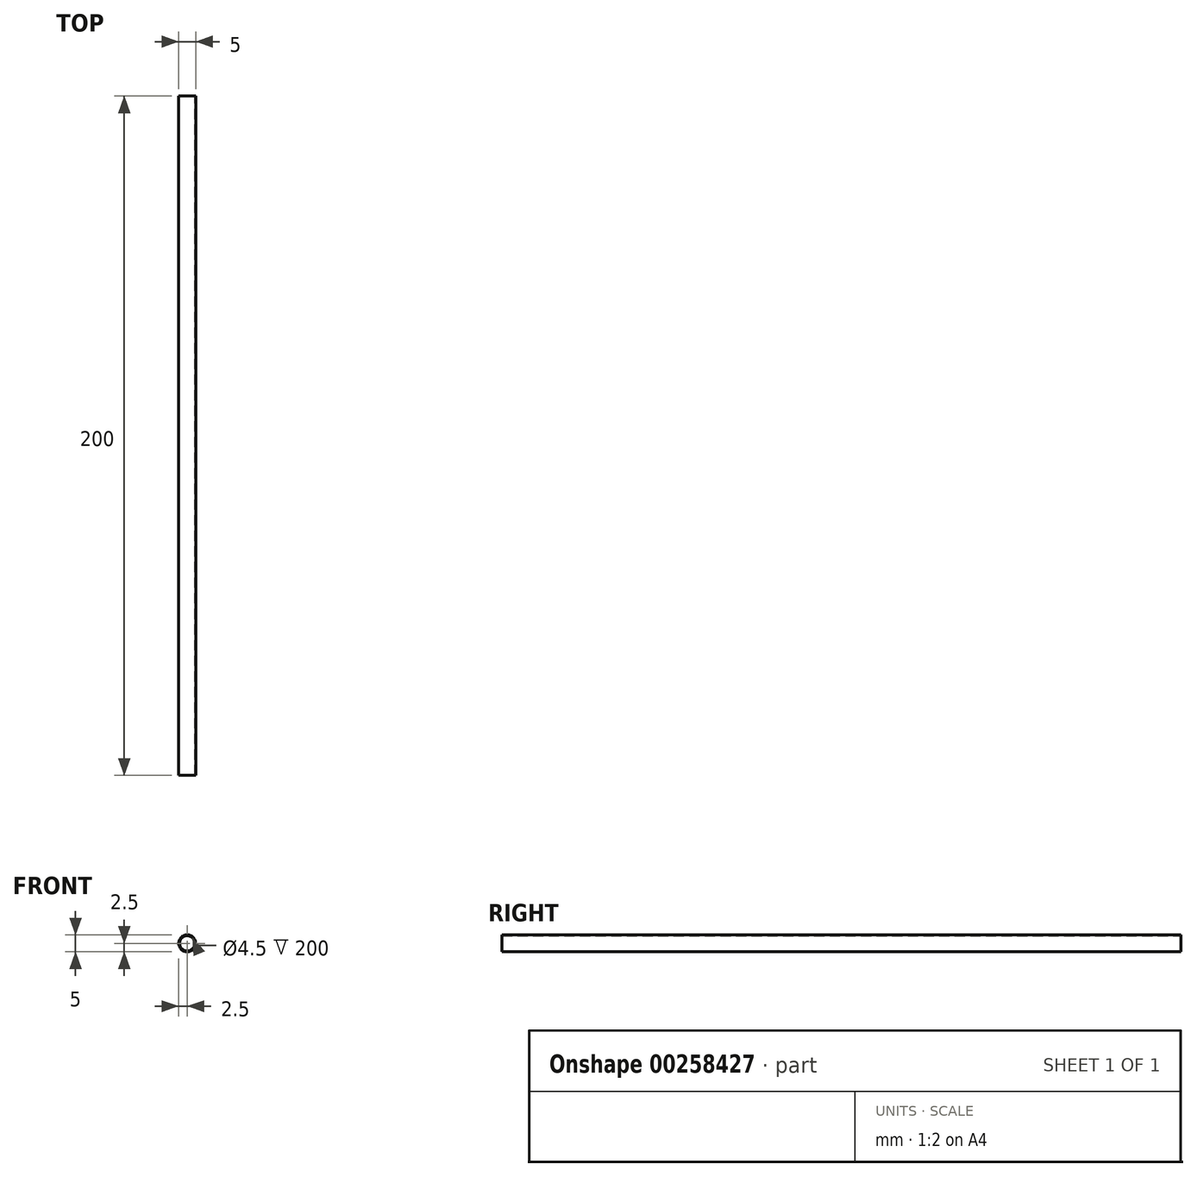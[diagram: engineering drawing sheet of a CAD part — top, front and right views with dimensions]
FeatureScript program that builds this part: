
annotation { "Feature Type Name" : "Feature", "Feature Type Description" : "" }
export const myFeature = defineFeature(function(context is Context, id is Id, definition is map)
    precondition{}
    {
        {
            var Q0;
            Q0=qCreatedBy(makeId("Front.planeOp"),FACE);
            var sketch = newSketch(context, id + "F0", { "sketchPlane" : qUnion([Q0])});
            skCircle(sketch, "E0", {"center": v(0, 0) * mm, "radius": 2.25 * mm});
            skCircle(sketch, "E1.0", {"center": v(0, 0) * mm, "radius": 2.5 * mm});
            skSolve(sketch);
        }
        {
            var Q0;
            Q0=makeQuery(id+"F0.imprint","IMPRINT",FACE,{"disambiguationData":[TD([[makeQuery(id+"F0.imprint","IMPRINT",EDGE,{"derivedFrom":sQuery(id+"F0.wireOp",EDGE,"E0")}),-1.0]])]});
            extrude(context, id + "F1", {"entities" : qUnion([Q0]), "depth" : 200 * mm, "symmetric" : true});
        }
    });
